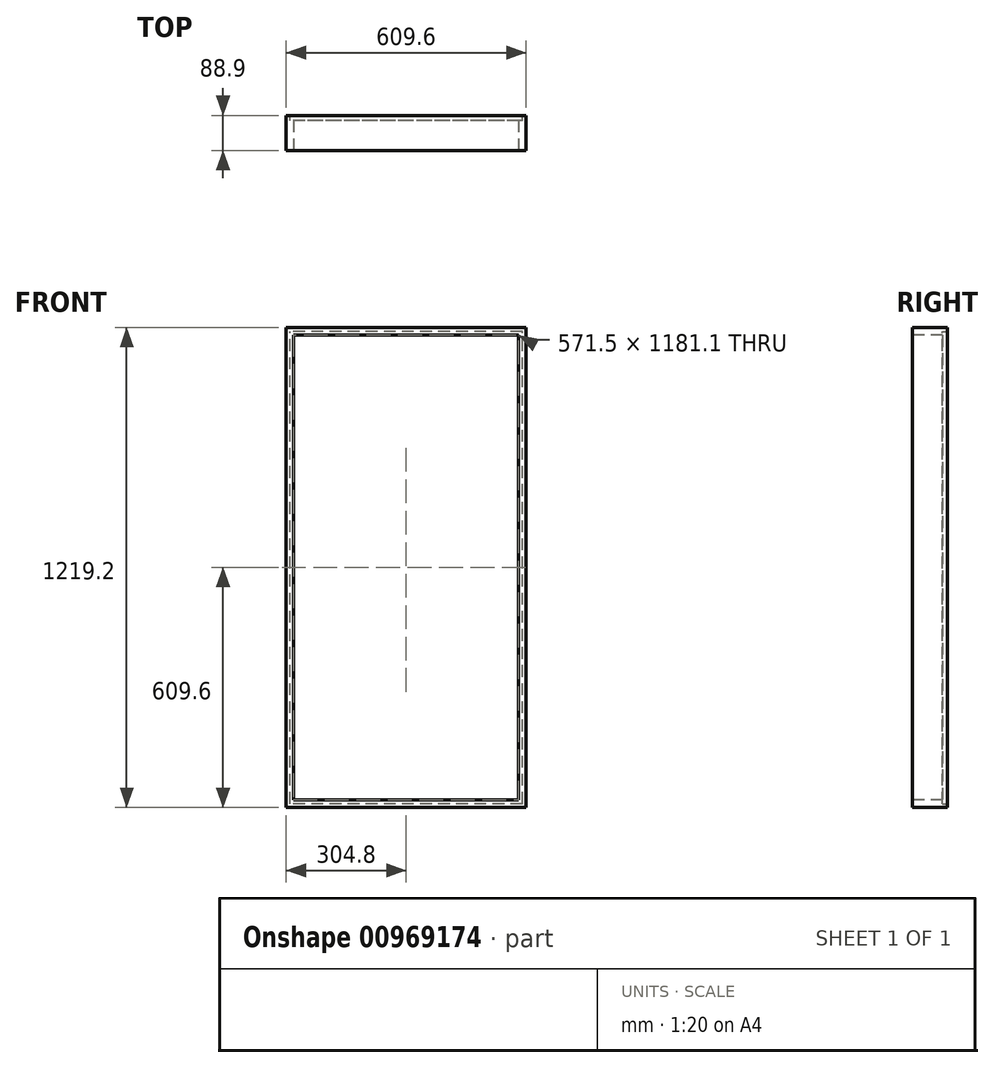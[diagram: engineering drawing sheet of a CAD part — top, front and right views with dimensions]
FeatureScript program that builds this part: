
annotation { "Feature Type Name" : "Feature", "Feature Type Description" : "" }
export const myFeature = defineFeature(function(context is Context, id is Id, definition is map)
    precondition{}
    {
        {
            var Q0;
            Q0=qCreatedBy(makeId("Front.planeOp"),FACE);
            var sketch = newSketch(context, id + "F0", { "sketchPlane" : qUnion([Q0])});
            skLineSegment(sketch, "E0.bottom", {"start": v(304.8, -609.6) * mm, "end": v(-304.8, -609.6) * mm});
            skLineSegment(sketch, "E0.top", {"start": v(304.8, 609.6) * mm, "end": v(-304.8, 609.6) * mm});
            skLineSegment(sketch, "E0.left", {"start": v(304.8, -609.6) * mm, "end": v(304.8, 609.6) * mm});
            skLineSegment(sketch, "E0.right", {"start": v(-304.8, -609.6) * mm, "end": v(-304.8, 609.6) * mm});
            skPoint(sketch, "E0.middle", {"position": v(0, 0) * mm});
            skSolve(sketch);
        }
        {
            var Q0;
            Q0 = qSketchRegion(id + "F0", true);
            extrude(context, id + "F1", {"entities" : qUnion([Q0]), "depth" : 88.9 * mm, "offsetDistance" : 25.4 * mm});
        }
        {
            var Q0;
            Q0=makeQuery(id+"F1.opExtrude","CAP_FACE",FACE,{"disambiguationData":[OSD([sQuery(id+"F0.wireOp",EDGE,"E0.bottom"),sQuery(id+"F0.wireOp",EDGE,"E0.top"),sQuery(id+"F0.wireOp",EDGE,"E0.left"),sQuery(id+"F0.wireOp",EDGE,"E0.right")])],"isStart":false});
            var sketch = newSketch(context, id + "F2", { "sketchPlane" : qUnion([Q0])});
            skLineSegment(sketch, "E1.bottom", {"start": v(285.75, 590.55) * mm, "end": v(-285.75, 590.55) * mm});
            skLineSegment(sketch, "E1.top", {"start": v(285.75, -590.55) * mm, "end": v(-285.75, -590.55) * mm});
            skLineSegment(sketch, "E1.left", {"start": v(285.75, 590.55) * mm, "end": v(285.75, -590.55) * mm});
            skLineSegment(sketch, "E1.right", {"start": v(-285.75, 590.55) * mm, "end": v(-285.75, -590.55) * mm});
            skPoint(sketch, "E1.middle", {"position": v(0, 0) * mm});
            skSolve(sketch);
        }
        {
            var Q0;
            Q0=makeQuery(id+"F2.imprint","IMPRINT",FACE,{"disambiguationData":[TD([[makeQuery(id+"F2.imprint","IMPRINT",EDGE,{"derivedFrom":sQuery(id+"F2.wireOp",EDGE,"E1.bottom")}),1.0]])]});
            extrude(context, id + "F3", {"entities" : qUnion([Q0]), "operationType" : NewBodyOperationType.REMOVE, "oppositeDirection" : true, "depth" : 88.9 * mm, "offsetDistance" : 25.4 * mm});
        }
        {
            var Q0;
            Q0=makeQuery(id+"F1.opExtrude","CAP_FACE",FACE,{"disambiguationData":[OSD([sQuery(id+"F0.wireOp",EDGE,"E0.bottom"),sQuery(id+"F0.wireOp",EDGE,"E0.top"),sQuery(id+"F0.wireOp",EDGE,"E0.left"),sQuery(id+"F0.wireOp",EDGE,"E0.right")])],"isStart":true});
            var sketch = newSketch(context, id + "F4", { "sketchPlane" : qUnion([Q0])});
            skLineSegment(sketch, "E2.bottom", {"start": v(-295.27, -600.08) * mm, "end": v(295.28, -600.08) * mm});
            skLineSegment(sketch, "E2.top", {"start": v(-295.28, 600.08) * mm, "end": v(295.27, 600.08) * mm});
            skLineSegment(sketch, "E2.left", {"start": v(-295.27, -600.08) * mm, "end": v(-295.28, 600.08) * mm});
            skLineSegment(sketch, "E2.right", {"start": v(295.28, -600.08) * mm, "end": v(295.27, 600.08) * mm});
            skPoint(sketch, "E2.middle", {"position": v(0, 0) * mm});
            skSolve(sketch);
        }
        {
            var Q0;
            Q0=makeQuery(id+"F4.imprint","IMPRINT",FACE,{"disambiguationData":[TD([[makeQuery(id+"F4.imprint","IMPRINT",EDGE,{"derivedFrom":sQuery(id+"F4.wireOp",EDGE,"E2.bottom")}),1.0]])]});
            extrude(context, id + "F5", {"entities" : qUnion([Q0]), "operationType" : NewBodyOperationType.REMOVE, "oppositeDirection" : true, "depth" : 12.7 * mm, "offsetDistance" : 25.4 * mm});
        }
    });
